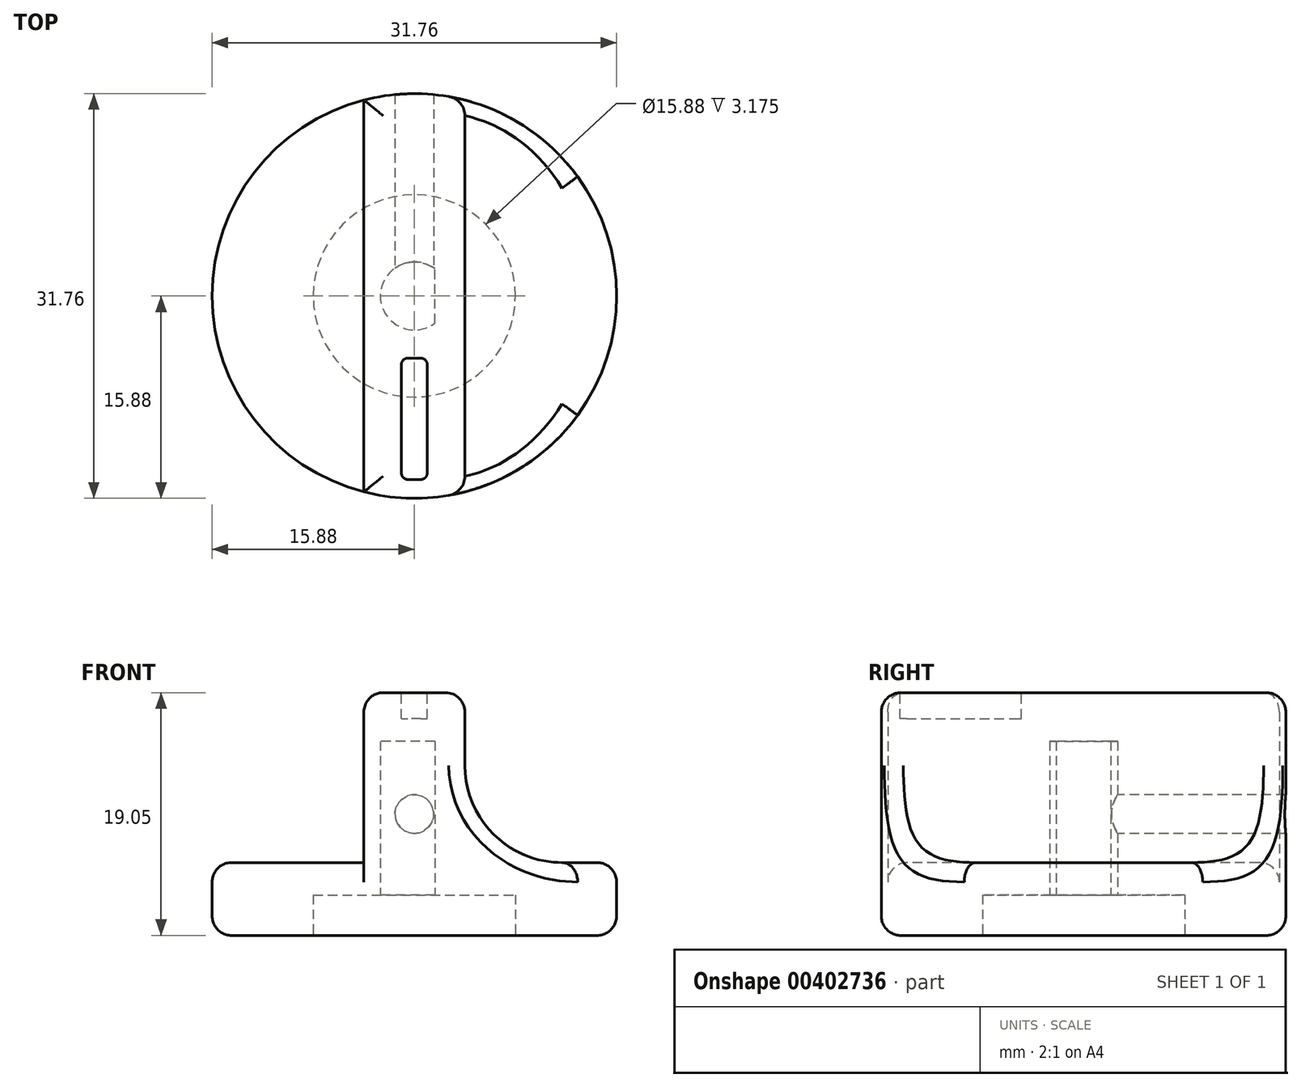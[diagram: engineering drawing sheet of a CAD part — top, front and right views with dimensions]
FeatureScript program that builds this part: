
annotation { "Feature Type Name" : "Feature", "Feature Type Description" : "" }
export const myFeature = defineFeature(function(context is Context, id is Id, definition is map)
    precondition{}
    {
        {
            var Q0;
            Q0=qCreatedBy(makeId("Top.planeOp"),FACE);
            var sketch = newSketch(context, id + "F0", { "sketchPlane" : qUnion([Q0])});
            skCircle(sketch, "E0", {"center": v(0, 0) * mm, "radius": 15.88 * mm});
            skSolve(sketch);
        }
        {
            var Q0;
            Q0=qSketchRegion(id+"F0",true);
            extrude(context, id + "F1", {"entities" : qUnion([Q0]), "depth" : 5.7 * mm});
        }
        {
            var Q0;
            Q0=makeQuery(id+"F1.opExtrude","CAP_FACE",FACE,{"disambiguationData":[OSD([sQuery(id+"F0.wireOp",EDGE,"E0")])],"isStart":false});
            var sketch = newSketch(context, id + "F2", { "sketchPlane" : qUnion([Q0])});
            skLineSegment(sketch, "E1.left", {"start": v(-3.97, 15.37) * mm, "end": v(-3.97, -15.37) * mm});
            skLineSegment(sketch, "E1.right", {"start": v(3.97, 15.37) * mm, "end": v(3.97, -15.37) * mm});
            skPoint(sketch, "E2", {"position": v(0, 23.82) * mm});
            skPoint(sketch, "E3", {"position": v(3.97, 0) * mm});
            skLineSegment(sketch, "E4", {"start": v(0, 34.26) * mm, "end": v(0, -28.44) * mm, "construction": true});
            skLineSegment(sketch, "E5", {"start": v(19.58, 0) * mm, "end": v(-22.13, 0) * mm, "construction": true});
            skArc(sketch, "E6.0", {"start": v(-3.97, -15.37) * mm, "mid": v(0, -15.88) * mm, "end": v(3.97, -15.37) * mm});
            skArc(sketch, "E7.trimOffspring", {"start": v(3.97, 15.37) * mm, "mid": v(0, 15.88) * mm, "end": v(-3.97, 15.37) * mm});
            skPoint(sketch, "E8.orphan", {"position": v(-3.97, 23.82) * mm});
            skPoint(sketch, "E1.bottom.end.orphan", {"position": v(3.97, 23.82) * mm});
            skPoint(sketch, "E9.orphan", {"position": v(3.97, -23.82) * mm});
            skSolve(sketch);
        }
        {
            var Q0;
            Q0=qSketchRegion(id+"F2",true);
            extrude(context, id + "F3", {"entities" : qUnion([Q0]), "operationType" : NewBodyOperationType.ADD, "depth" : 13.33 * mm});
        }
        {
            var Q0;
            Q0=makeQuery(id+"F3.opExtrude","CAP_FACE",FACE,{"disambiguationData":[OSD([sQuery(id+"F2.wireOp",EDGE,"E1.left"),sQuery(id+"F2.wireOp",EDGE,"E1.right"),sQuery(id+"F2.wireOp",EDGE,"E6.0"),sQuery(id+"F2.wireOp",EDGE,"E7.trimOffspring")])],"isStart":false});
            var sketch = newSketch(context, id + "F4", { "sketchPlane" : qUnion([Q0])});
            skLineSegment(sketch, "E10.bottom", {"start": v(0.5, -14.4) * mm, "end": v(-0.5, -14.4) * mm});
            skLineSegment(sketch, "E10.top", {"start": v(0.5, -4.88) * mm, "end": v(-0.5, -4.88) * mm});
            skLineSegment(sketch, "E10.left", {"start": v(1.02, -13.9) * mm, "end": v(1.02, -5.38) * mm});
            skLineSegment(sketch, "E10.right", {"start": v(-1.02, -13.9) * mm, "end": v(-1.02, -5.38) * mm});
            skPoint(sketch, "E11", {"position": v(0, -14.4) * mm});
            skLineSegment(sketch, "E12", {"start": v(0, -16.34) * mm, "end": v(0, 0) * mm, "construction": true});
            skPoint(sketch, "E13.visualSharp", {"position": v(1.02, -14.4) * mm});
            skArc(sketch, "E13.filletArc", {"start": v(0.5, -14.4) * mm, "mid": v(0.87, -14.25) * mm, "end": v(1.02, -13.9) * mm});
            skPoint(sketch, "E14.visualSharp", {"position": v(-1.02, -14.4) * mm});
            skArc(sketch, "E14.filletArc", {"start": v(-1.02, -13.9) * mm, "mid": v(-0.87, -14.25) * mm, "end": v(-0.5, -14.4) * mm});
            skPoint(sketch, "E15.visualSharp", {"position": v(-1.02, -4.88) * mm});
            skArc(sketch, "E15.filletArc", {"start": v(-0.5, -4.88) * mm, "mid": v(-0.87, -5.03) * mm, "end": v(-1.02, -5.38) * mm});
            skPoint(sketch, "E16.visualSharp", {"position": v(1.02, -4.88) * mm});
            skArc(sketch, "E16.filletArc", {"start": v(1.02, -5.38) * mm, "mid": v(0.87, -5.03) * mm, "end": v(0.5, -4.88) * mm});
            skSolve(sketch);
        }
        {
            var Q0;
            Q0=makeQuery(id+"F3.opExtrude","CAP_EDGE",EDGE,{"disambiguationData":[OSD([sQuery(id+"F2.wireOp",EDGE,"E1.left")])],"isStart":true});
            var Q1;
            Q1=makeQuery(id+"F3.opExtrude","CAP_EDGE",EDGE,{"disambiguationData":[OSD([sQuery(id+"F2.wireOp",EDGE,"E1.right")])],"isStart":true});
            fillet(context, id + "F5", {"entities" : qUnion([Q0, Q1]), "radius" : 7.62 * mm, "tangentPropagation" : true, "allowEdgeOverflow" : false});
        }
        {
            var Q0;
            {var subQ0=sQuery(id+"F0.wireOp",EDGE,"E0");Q0=makeQuery(id+"F3.boolean.opBoolean","SPLIT",EDGE,{"disambiguationData":[TD([makeQuery(id+"F3.opExtrude","SWEPT_FACE",FACE,{"disambiguationData":[OSD([sQuery(id+"F2.wireOp",EDGE,"E1.left")])]})])],"derivedFrom":makeQuery(id+"F1.opExtrude","CAP_EDGE",EDGE,{"disambiguationData":[OSD([subQ0])],"isStart":false})});}
            var Q1;
            {var subQ0=sQuery(id+"F0.wireOp",EDGE,"E0");Q1=makeQuery(id+"F3.boolean.opBoolean","SPLIT",EDGE,{"disambiguationData":[TD([makeQuery(id+"F3.opExtrude","SWEPT_FACE",FACE,{"disambiguationData":[OSD([sQuery(id+"F2.wireOp",EDGE,"E1.right")])]})])],"derivedFrom":makeQuery(id+"F1.opExtrude","CAP_EDGE",EDGE,{"disambiguationData":[OSD([subQ0])],"isStart":false})});}
            var Q2;
            Q2=makeQuery(id+"F3.opExtrude","CAP_EDGE",EDGE,{"disambiguationData":[OSD([sQuery(id+"F2.wireOp",EDGE,"E6.0")])],"isStart":false});
            var Q3;
            Q3=makeQuery(id+"F3.opExtrude","CAP_EDGE",EDGE,{"disambiguationData":[OSD([sQuery(id+"F2.wireOp",EDGE,"E1.left")])],"isStart":false});
            var Q4;
            Q4=makeQuery(id+"F3.opExtrude","CAP_EDGE",EDGE,{"disambiguationData":[OSD([sQuery(id+"F2.wireOp",EDGE,"E1.right")])],"isStart":false});
            var Q5;
            Q5=makeQuery(id+"F3.opExtrude","CAP_EDGE",EDGE,{"disambiguationData":[OSD([sQuery(id+"F2.wireOp",EDGE,"E7.trimOffspring")])],"isStart":false});
            var Q6;
            Q6=makeQuery(id+"F1.opExtrude","CAP_EDGE",EDGE,{"disambiguationData":[OSD([sQuery(id+"F0.wireOp",EDGE,"E0")])],"isStart":true});
            fillet(context, id + "F6", {"entities" : qUnion([Q0, Q1, Q2, Q3, Q4, Q5, Q6]), "radius" : 1.52 * mm, "tangentPropagation" : true, "allowEdgeOverflow" : false});
        }
        {
            var Q0;
            Q0=makeQuery(id+"F1.opExtrude","CAP_FACE",FACE,{"disambiguationData":[OSD([sQuery(id+"F0.wireOp",EDGE,"E0")])],"isStart":true});
            var sketch = newSketch(context, id + "F7", { "sketchPlane" : qUnion([Q0])});
            skLineSegment(sketch, "E17", {"start": v(1.6, -5) * mm, "end": v(1.6, 4.02) * mm, "construction": true});
            skLineSegment(sketch, "E18", {"start": v(1.6, -2.13) * mm, "end": v(1.6, 2.13) * mm});
            skArc(sketch, "E19.MirrorCS", {"start": v(1.6, -2.13) * mm, "mid": v(-2.67, 0) * mm, "end": v(1.6, 2.13) * mm});
            skSolve(sketch);
        }
        {
            var Q0;
            Q0=qSketchRegion(id+"F7",true);
            extrude(context, id + "F8", {"entities" : qUnion([Q0]), "operationType" : NewBodyOperationType.REMOVE, "oppositeDirection" : true, "depth" : 15.24 * mm});
        }
        {
            var Q0;
            Q0=qSketchRegion(id+"F4",true);
            extrude(context, id + "F9", {"entities" : qUnion([Q0]), "operationType" : NewBodyOperationType.REMOVE, "oppositeDirection" : true, "depth" : 2.03 * mm});
        }
        {
            var Q0;
            Q0=qCreatedBy(makeId("Front.planeOp"),FACE);
            var sketch = newSketch(context, id + "F10", { "sketchPlane" : qUnion([Q0])});
            skCircle(sketch, "E20", {"center": v(0, 9.53) * mm, "radius": 1.52 * mm});
            skSolve(sketch);
        }
        {
            var Q0;
            Q0=qSketchRegion(id+"F10",true);
            extrude(context, id + "F11", {"entities" : qUnion([Q0]), "operationType" : NewBodyOperationType.REMOVE, "endBound" : BoundingType.THROUGH_ALL, "oppositeDirection" : true, "depth" : 25.4 * mm});
        }
        {
            var Q0;
            Q0=makeQuery(id+"F1.opExtrude","CAP_FACE",FACE,{"disambiguationData":[OSD([sQuery(id+"F0.wireOp",EDGE,"E0")])],"isStart":true});
            var sketch = newSketch(context, id + "F12", { "sketchPlane" : qUnion([Q0])});
            skCircle(sketch, "E21", {"center": v(0, 0) * mm, "radius": 7.94 * mm});
            skSolve(sketch);
        }
        {
            var Q0;
            Q0=qSketchRegion(id+"F12",true);
            extrude(context, id + "F13", {"entities" : qUnion([Q0]), "operationType" : NewBodyOperationType.REMOVE, "oppositeDirection" : true, "depth" : 3.17 * mm});
        }
    });
